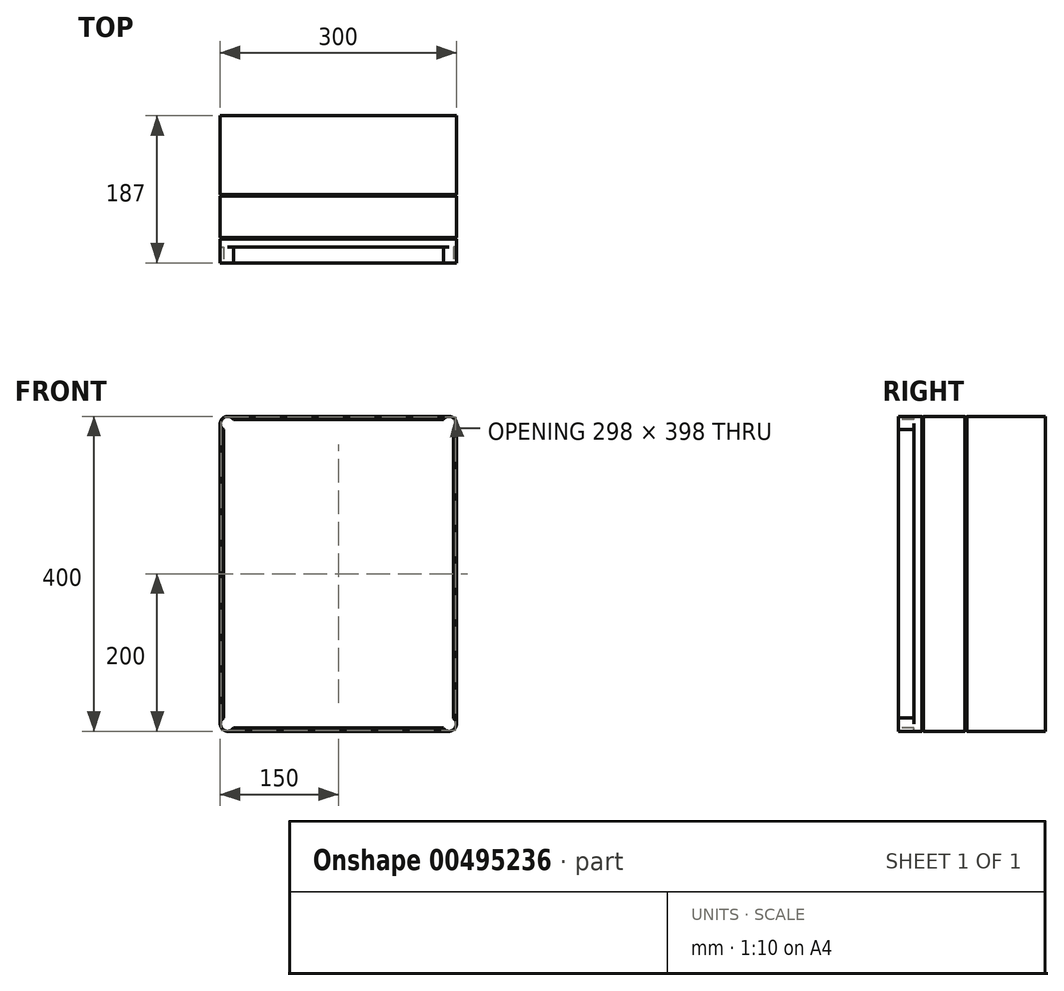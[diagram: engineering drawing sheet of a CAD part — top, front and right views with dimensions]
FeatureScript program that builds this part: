
annotation { "Feature Type Name" : "Feature", "Feature Type Description" : "" }
export const myFeature = defineFeature(function(context is Context, id is Id, definition is map)
    precondition{}
    {
        {
            var Q0;
            Q0=qCreatedBy(makeId("Front.planeOp"),FACE);
            var sketch = newSketch(context, id + "F0", { "sketchPlane" : qUnion([Q0])});
            skLineSegment(sketch, "E0.bottom", {"start": v(-140.9, 200) * mm, "end": v(140.9, 200) * mm});
            skLineSegment(sketch, "E0.top", {"start": v(-140.9, -200) * mm, "end": v(140.9, -200) * mm});
            skLineSegment(sketch, "E0.left", {"start": v(-150, 190.9) * mm, "end": v(-150, -190.9) * mm});
            skLineSegment(sketch, "E0.right", {"start": v(150, 190.9) * mm, "end": v(150, -190.9) * mm});
            skPoint(sketch, "E0.middle", {"position": v(0, 0) * mm});
            skPoint(sketch, "E1.visualSharp", {"position": v(-150, 200) * mm});
            skArc(sketch, "E1.filletArc", {"start": v(-140.9, 200) * mm, "mid": v(-147.33, 197.33) * mm, "end": v(-150, 190.9) * mm});
            skPoint(sketch, "E2.visualSharp", {"position": v(150, 200) * mm});
            skArc(sketch, "E2.filletArc", {"start": v(150, 190.9) * mm, "mid": v(147.33, 197.33) * mm, "end": v(140.9, 200) * mm});
            skPoint(sketch, "E3.visualSharp", {"position": v(-150, -200) * mm});
            skArc(sketch, "E3.filletArc", {"start": v(-150, -190.9) * mm, "mid": v(-147.33, -197.33) * mm, "end": v(-140.9, -200) * mm});
            skPoint(sketch, "E4.visualSharp", {"position": v(150, -200) * mm});
            skArc(sketch, "E4.filletArc", {"start": v(140.9, -200) * mm, "mid": v(147.33, -197.33) * mm, "end": v(150, -190.9) * mm});
            skSolve(sketch);
        }
        {
            var Q0;
            Q0 = qSketchRegion(id + "F0", true);
            extrude(context, id + "F1", {"entities" : qUnion([Q0]), "depth" : 100 * mm});
        }
        {
            var Q0;
            Q0=makeQuery(id+"F1.opExtrude","CAP_FACE",FACE,{"disambiguationData":[OSD([sQuery(id+"F0.wireOp",EDGE,"E0.bottom"),sQuery(id+"F0.wireOp",EDGE,"E0.top"),sQuery(id+"F0.wireOp",EDGE,"E0.left"),sQuery(id+"F0.wireOp",EDGE,"E0.right")])],"isStart":false});
            var sketch = newSketch(context, id + "F2", { "sketchPlane" : qUnion([Q0])});
            skLineSegment(sketch, "E5.0.0", {"start": v(-150, 190.9) * mm, "end": v(-150, -190.9) * mm});
            skLineSegment(sketch, "E5.0.1", {"start": v(-140.9, -200) * mm, "end": v(-140.9, -200) * mm});
            skLineSegment(sketch, "E5.0.2", {"start": v(150, -190.9) * mm, "end": v(150, 190.9) * mm});
            skLineSegment(sketch, "E5.0.3", {"start": v(140.9, 200) * mm, "end": v(-140.9, 200) * mm});
            skLineSegment(sketch, "E6.0", {"start": v(139.9, 199) * mm, "end": v(-139.9, 199) * mm});
            skLineSegment(sketch, "E6.1", {"start": v(149, -189.9) * mm, "end": v(149, 189.9) * mm});
            skLineSegment(sketch, "E6.2", {"start": v(-139.9, -199) * mm, "end": v(139.9, -199) * mm});
            skLineSegment(sketch, "E6.3", {"start": v(-149, 189.9) * mm, "end": v(-149, -189.9) * mm});
            skPoint(sketch, "E7.visualSharp", {"position": v(-149, 199) * mm});
            skArc(sketch, "E7.filletArc", {"start": v(-139.9, 199) * mm, "mid": v(-146.33, 196.33) * mm, "end": v(-149, 189.9) * mm});
            skPoint(sketch, "E8.newPointB", {"position": v(-150, 190.9) * mm});
            skArc(sketch, "E8.filletArc", {"start": v(-140.9, 200) * mm, "mid": v(-147.33, 197.33) * mm, "end": v(-150, 190.9) * mm});
            skPoint(sketch, "E9.visualSharp", {"position": v(149, 199) * mm});
            skArc(sketch, "E9.filletArc", {"start": v(149, 189.9) * mm, "mid": v(146.33, 196.33) * mm, "end": v(139.9, 199) * mm});
            skPoint(sketch, "E10.newPointA", {"position": v(150, 190.9) * mm});
            skArc(sketch, "E10.filletArc", {"start": v(150, 190.9) * mm, "mid": v(147.33, 197.33) * mm, "end": v(140.9, 200) * mm});
            skPoint(sketch, "E11.visualSharp", {"position": v(149, -199) * mm});
            skArc(sketch, "E11.filletArc", {"start": v(139.9, -199) * mm, "mid": v(146.33, -196.33) * mm, "end": v(149, -189.9) * mm});
            skPoint(sketch, "E12.visualSharp", {"position": v(-149, -199) * mm});
            skArc(sketch, "E12.filletArc", {"start": v(-149, -189.9) * mm, "mid": v(-146.33, -196.33) * mm, "end": v(-139.9, -199) * mm});
            skPoint(sketch, "E13.newPointA", {"position": v(-150, -190.9) * mm});
            skArc(sketch, "E13.filletArc", {"start": v(-150, -190.9) * mm, "mid": v(-147.33, -197.33) * mm, "end": v(-140.9, -200) * mm});
            skLineSegment(sketch, "E14.0", {"start": v(-140.9, -200) * mm, "end": v(140.9, -200) * mm});
            skPoint(sketch, "E15.newPointA", {"position": v(140.9, -200) * mm});
            skArc(sketch, "E15.filletArc", {"start": v(140.9, -200) * mm, "mid": v(147.33, -197.33) * mm, "end": v(150, -190.9) * mm});
            skSolve(sketch);
        }
        {
            var Q0;
            Q0=makeQuery(id+"F2.imprint","IMPRINT",FACE,{"disambiguationData":[TD([[makeQuery(id+"F2.imprint","IMPRINT",EDGE,{"derivedFrom":sQuery(id+"F2.wireOp",EDGE,"E6.0")}),1.0]])]});
            extrude(context, id + "F3", {"entities" : qUnion([Q0]), "operationType" : NewBodyOperationType.ADD, "depth" : 2 * mm});
        }
        {
            var Q0;
            Q0=makeQuery(id+"F3.opExtrude","CAP_FACE",FACE,{"disambiguationData":[OSD([sQuery(id+"F2.wireOp",EDGE,"E6.0"),sQuery(id+"F2.wireOp",EDGE,"E6.1"),sQuery(id+"F2.wireOp",EDGE,"E6.2"),sQuery(id+"F2.wireOp",EDGE,"E6.3")])],"isStart":false});
            var sketch = newSketch(context, id + "F4", { "sketchPlane" : qUnion([Q0])});
            skArc(sketch, "E16.0.0", {"start": v(-150, -190.9) * mm, "mid": v(-147.33, -197.33) * mm, "end": v(-140.9, -200) * mm});
            skLineSegment(sketch, "E16.0.1", {"start": v(-140.9, -200) * mm, "end": v(140.9, -200) * mm});
            skArc(sketch, "E16.0.2", {"start": v(140.9, -200) * mm, "mid": v(147.33, -197.33) * mm, "end": v(150, -190.9) * mm});
            skLineSegment(sketch, "E16.0.3", {"start": v(150, -190.9) * mm, "end": v(150, 190.9) * mm});
            skArc(sketch, "E16.0.4", {"start": v(150, 190.9) * mm, "mid": v(147.33, 197.33) * mm, "end": v(140.9, 200) * mm});
            skLineSegment(sketch, "E16.0.5", {"start": v(140.9, 200) * mm, "end": v(-140.9, 200) * mm});
            skArc(sketch, "E16.0.6", {"start": v(-140.9, 200) * mm, "mid": v(-147.33, 197.33) * mm, "end": v(-150, 190.9) * mm});
            skLineSegment(sketch, "E16.0.7", {"start": v(-150, 190.9) * mm, "end": v(-150, -190.9) * mm});
            skSolve(sketch);
        }
        {
            var Q0;
            Q0=makeQuery(id+"F4.imprint","IMPRINT",FACE,{"disambiguationData":[TD([[makeQuery(id+"F4.imprint","IMPRINT",EDGE,{"derivedFrom":sQuery(id+"F4.wireOp",EDGE,"E16.0.0")}),1.0]])]});
            var Q1;
            Q1=makeQuery(id+"F4.imprint","IMPRINT",FACE,{"disambiguationData":[TD([[makeQuery(id+"F4.imprint","IMPRINT",EDGE,{"derivedFrom":makeQuery(id+"F3.opExtrude","CAP_EDGE",EDGE,{"disambiguationData":[OSD([sQuery(id+"F2.wireOp",EDGE,"E6.0")])],"isStart":false})}),1.0]])]});
            extrude(context, id + "F5", {"entities" : qUnion([Q0, Q1]), "depth" : 53 * mm});
        }
        {
            var Q0;
            Q0=makeQuery(id+"F5.opExtrude","CAP_FACE",FACE,{"disambiguationData":[OSD([sQuery(id+"F4.wireOp",EDGE,"E16.0.0"),sQuery(id+"F4.wireOp",EDGE,"E16.0.1"),sQuery(id+"F4.wireOp",EDGE,"E16.0.2"),sQuery(id+"F4.wireOp",EDGE,"E16.0.3"),sQuery(id+"F4.wireOp",EDGE,"E16.0.4"),sQuery(id+"F4.wireOp",EDGE,"E16.0.5"),sQuery(id+"F4.wireOp",EDGE,"E16.0.6"),sQuery(id+"F4.wireOp",EDGE,"E16.0.7")])],"isStart":false});
            var sketch = newSketch(context, id + "F6", { "sketchPlane" : qUnion([Q0])});
            skArc(sketch, "E17.0", {"start": v(-139.9, 199) * mm, "mid": v(-146.33, 196.33) * mm, "end": v(-149, 189.9) * mm});
            skLineSegment(sketch, "E17.1", {"start": v(139.9, 199) * mm, "end": v(-139.9, 199) * mm});
            skLineSegment(sketch, "E17.2", {"start": v(-149, 189.9) * mm, "end": v(-149, -189.9) * mm});
            skArc(sketch, "E17.3", {"start": v(149, 189.9) * mm, "mid": v(146.33, 196.33) * mm, "end": v(139.9, 199) * mm});
            skLineSegment(sketch, "E17.4", {"start": v(149, -189.9) * mm, "end": v(149, 189.9) * mm});
            skArc(sketch, "E17.5", {"start": v(-149, -189.9) * mm, "mid": v(-146.33, -196.33) * mm, "end": v(-139.9, -199) * mm});
            skLineSegment(sketch, "E17.6", {"start": v(-139.9, -199) * mm, "end": v(139.9, -199) * mm});
            skArc(sketch, "E17.7", {"start": v(139.9, -199) * mm, "mid": v(146.33, -196.33) * mm, "end": v(149, -189.9) * mm});
            skSolve(sketch);
        }
        {
            var Q0;
            Q0=makeQuery(id+"F6.imprint","IMPRINT",FACE,{"disambiguationData":[TD([[makeQuery(id+"F6.imprint","IMPRINT",EDGE,{"derivedFrom":sQuery(id+"F6.wireOp",EDGE,"E17.0")}),1.0]])]});
            extrude(context, id + "F7", {"entities" : qUnion([Q0]), "operationType" : NewBodyOperationType.ADD, "depth" : 2 * mm});
        }
        {
            var Q0;
            Q0=makeQuery(id+"F7.opExtrude","CAP_FACE",FACE,{"disambiguationData":[OSD([sQuery(id+"F6.wireOp",EDGE,"E17.0"),sQuery(id+"F6.wireOp",EDGE,"E17.1"),sQuery(id+"F6.wireOp",EDGE,"E17.2"),sQuery(id+"F6.wireOp",EDGE,"E17.3"),sQuery(id+"F6.wireOp",EDGE,"E17.4"),sQuery(id+"F6.wireOp",EDGE,"E17.5"),sQuery(id+"F6.wireOp",EDGE,"E17.6"),sQuery(id+"F6.wireOp",EDGE,"E17.7")])],"isStart":false});
            var sketch = newSketch(context, id + "F8", { "sketchPlane" : qUnion([Q0])});
            skLineSegment(sketch, "E18.bottom", {"start": v(145, 195) * mm, "end": v(-145, 195) * mm});
            skLineSegment(sketch, "E18.top", {"start": v(145, -195) * mm, "end": v(-145, -195) * mm});
            skLineSegment(sketch, "E18.left", {"start": v(145, 195) * mm, "end": v(145, -195) * mm});
            skLineSegment(sketch, "E18.right", {"start": v(-145, 195) * mm, "end": v(-145, -195) * mm});
            skPoint(sketch, "E18.middle", {"position": v(0, 0) * mm});
            skArc(sketch, "E19.0.0", {"start": v(-140.9, 200) * mm, "mid": v(-147.33, 197.33) * mm, "end": v(-150, 190.9) * mm});
            skLineSegment(sketch, "E19.0.1", {"start": v(-150, 190.9) * mm, "end": v(-150, -190.9) * mm});
            skArc(sketch, "E19.0.2", {"start": v(-150, -190.9) * mm, "mid": v(-147.33, -197.33) * mm, "end": v(-140.9, -200) * mm});
            skLineSegment(sketch, "E19.0.3", {"start": v(-140.9, -200) * mm, "end": v(140.9, -200) * mm});
            skArc(sketch, "E19.0.4", {"start": v(140.9, -200) * mm, "mid": v(147.33, -197.33) * mm, "end": v(150, -190.9) * mm});
            skLineSegment(sketch, "E19.0.5", {"start": v(150, -190.9) * mm, "end": v(150, 190.9) * mm});
            skArc(sketch, "E19.0.6", {"start": v(150, 190.9) * mm, "mid": v(147.33, 197.33) * mm, "end": v(140.9, 200) * mm});
            skLineSegment(sketch, "E19.0.7", {"start": v(140.9, 200) * mm, "end": v(-140.9, 200) * mm});
            skSolve(sketch);
        }
        {
            var Q0;
            Q0=makeQuery(id+"F8.imprint","IMPRINT",FACE,{"disambiguationData":[TD([[makeQuery(id+"F8.imprint","IMPRINT",EDGE,{"derivedFrom":sQuery(id+"F8.wireOp",EDGE,"E19.0.0")}),1.0]])]});
            var Q1;
            Q1=makeQuery(id+"F8.imprint","IMPRINT",FACE,{"disambiguationData":[TD([[makeQuery(id+"F8.imprint","IMPRINT",EDGE,{"derivedFrom":sQuery(id+"F8.wireOp",EDGE,"E18.bottom")}),-1.0]])]});
            var Q2;
            Q2=makeQuery(id+"F8.imprint","IMPRINT",FACE,{"disambiguationData":[TD([[makeQuery(id+"F8.imprint","IMPRINT",EDGE,{"derivedFrom":sQuery(id+"F8.wireOp",EDGE,"E18.bottom")}),1.0]])]});
            extrude(context, id + "F9", {"entities" : qUnion([Q0, Q1, Q2]), "depth" : 30 * mm});
        }
        {
            var Q0;
            Q0=makeQuery(id+"F9.opExtrude","CAP_FACE",FACE,{"disambiguationData":[OSD([sQuery(id+"F8.wireOp",EDGE,"E19.0.0"),sQuery(id+"F8.wireOp",EDGE,"E19.0.1"),sQuery(id+"F8.wireOp",EDGE,"E19.0.2"),sQuery(id+"F8.wireOp",EDGE,"E19.0.3"),sQuery(id+"F8.wireOp",EDGE,"E19.0.4"),sQuery(id+"F8.wireOp",EDGE,"E19.0.5"),sQuery(id+"F8.wireOp",EDGE,"E19.0.6"),sQuery(id+"F8.wireOp",EDGE,"E19.0.7")])],"isStart":false});
            var sketch = newSketch(context, id + "F10", { "sketchPlane" : qUnion([Q0])});
            skArc(sketch, "E20.0.0", {"start": v(150, 190.9) * mm, "mid": v(147.33, 197.33) * mm, "end": v(140.9, 200) * mm, "construction": true});
            skLineSegment(sketch, "E20.0.1", {"start": v(140.9, 200) * mm, "end": v(-140.9, 200) * mm, "construction": true});
            skArc(sketch, "E20.0.2", {"start": v(-140.9, 200) * mm, "mid": v(-147.33, 197.33) * mm, "end": v(-150, 190.9) * mm, "construction": true});
            skLineSegment(sketch, "E20.0.3", {"start": v(-150, 190.9) * mm, "end": v(-150, -190.9) * mm, "construction": true});
            skArc(sketch, "E20.0.4", {"start": v(-150, -190.9) * mm, "mid": v(-147.33, -197.33) * mm, "end": v(-140.9, -200) * mm, "construction": true});
            skLineSegment(sketch, "E20.0.5", {"start": v(-140.9, -200) * mm, "end": v(140.9, -200) * mm, "construction": true});
            skArc(sketch, "E20.0.6", {"start": v(140.9, -200) * mm, "mid": v(147.33, -197.33) * mm, "end": v(150, -190.9) * mm, "construction": true});
            skLineSegment(sketch, "E20.0.7", {"start": v(150, -190.9) * mm, "end": v(150, 190.9) * mm, "construction": true});
            skLineSegment(sketch, "E21.bottom", {"start": v(-133, 200) * mm, "end": v(133, 200) * mm});
            skLineSegment(sketch, "E21.top", {"start": v(-133.36, 196) * mm, "end": v(133.36, 196) * mm});
            skPoint(sketch, "E22.middle", {"position": v(0, 0) * mm});
            skCircle(sketch, "E23", {"center": v(-140.9, 190.9) * mm, "radius": 9.1 * mm});
            skCircle(sketch, "E24", {"center": v(140.9, 190.9) * mm, "radius": 9.1 * mm});
            skCircle(sketch, "E25.MirrorC", {"center": v(-140.9, -190.9) * mm, "radius": 9.1 * mm});
            skLineSegment(sketch, "E26.MirrorCS", {"start": v(-133.36, -196) * mm, "end": v(133.36, -196) * mm});
            skCircle(sketch, "E27.MirrorC", {"center": v(140.9, -190.9) * mm, "radius": 9.1 * mm});
            skLineSegment(sketch, "E28.0", {"start": v(-146, 183.36) * mm, "end": v(-146, -183.36) * mm});
            skLineSegment(sketch, "E29.0", {"start": v(146, -183.36) * mm, "end": v(146, 183.36) * mm});
            skSolve(sketch);
        }
        {
            var Q0;
            {var subQ6=sQuery(id+"F10.wireOp",EDGE,"E21.bottom");Q0=makeQuery(id+"F10.imprint","IMPRINT",FACE,{"disambiguationData":[TD([[makeQuery(id+"F10.imprint","IMPRINT",EDGE,{"derivedFrom":subQ6}),1.0]])]});}
            var Q1;
            {var subQ2=sQuery(id+"F10.wireOp",EDGE,"E28.0");Q1=makeQuery(id+"F10.imprint","IMPRINT",FACE,{"disambiguationData":[TD([[makeQuery(id+"F10.imprint","IMPRINT",EDGE,{"derivedFrom":subQ2}),-1.0]])]});}
            var Q2;
            {var subQ2=sQuery(id+"F10.wireOp",EDGE,"E29.0");Q2=makeQuery(id+"F10.imprint","IMPRINT",FACE,{"disambiguationData":[TD([[makeQuery(id+"F10.imprint","IMPRINT",EDGE,{"derivedFrom":subQ2}),-1.0]])]});}
            var Q3;
            {var subQ2=sQuery(id+"F10.wireOp",EDGE,"E26.MirrorCS");Q3=makeQuery(id+"F10.imprint","IMPRINT",FACE,{"disambiguationData":[TD([[makeQuery(id+"F10.imprint","IMPRINT",EDGE,{"derivedFrom":subQ2}),-1.0]])]});}
            extrude(context, id + "F11", {"entities" : qUnion([Q0, Q1, Q2, Q3]), "operationType" : NewBodyOperationType.REMOVE, "oppositeDirection" : true, "depth" : 20 * mm});
        }
    });
